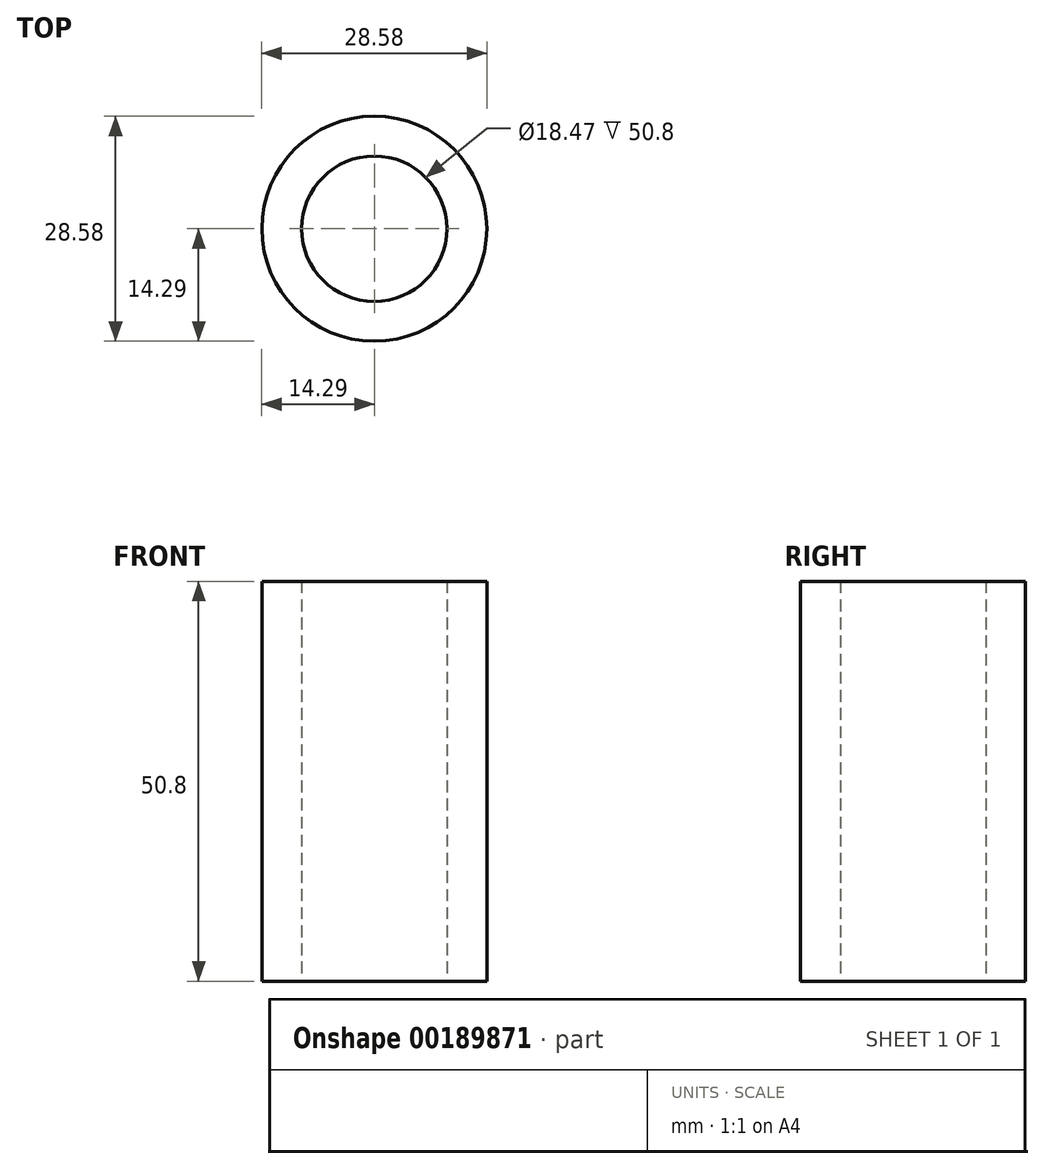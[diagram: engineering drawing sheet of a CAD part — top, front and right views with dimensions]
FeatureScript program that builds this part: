
annotation { "Feature Type Name" : "Feature", "Feature Type Description" : "" }
export const myFeature = defineFeature(function(context is Context, id is Id, definition is map)
    precondition{}
    {
        {
            var Q0;
            Q0=qCreatedBy(makeId("Top.planeOp"),FACE);
            var sketch = newSketch(context, id + "F0", { "sketchPlane" : qUnion([Q0])});
            skCircle(sketch, "E0", {"center": v(0, 0) * mm, "radius": 14.29 * mm});
            skCircle(sketch, "E1", {"center": v(0, 0) * mm, "radius": 9.23 * mm});
            skSolve(sketch);
        }
        {
            var Q0;
            Q0 = qSketchRegion(id + "F0", true);
            extrude(context, id + "F1", {"entities" : qUnion([Q0]), "depth" : 50.8 * mm});
        }
    });
